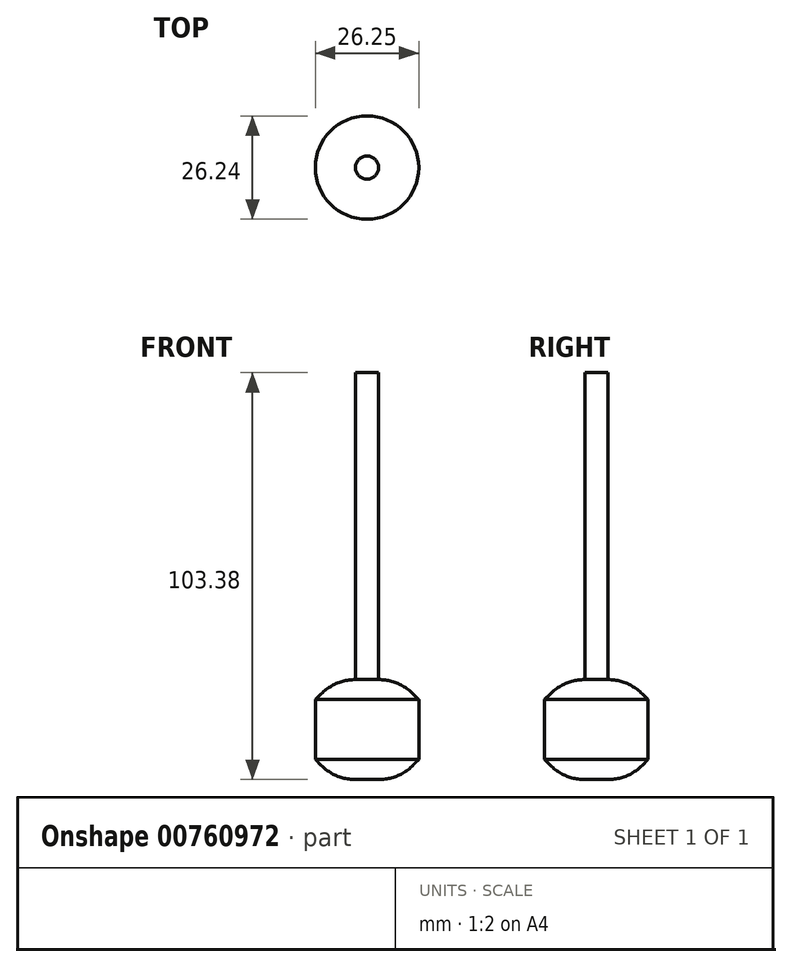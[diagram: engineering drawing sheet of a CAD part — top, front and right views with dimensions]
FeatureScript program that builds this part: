
annotation { "Feature Type Name" : "Feature", "Feature Type Description" : "" }
export const myFeature = defineFeature(function(context is Context, id is Id, definition is map)
    precondition{}
    {
        {
            var Q0;
            Q0=qCreatedBy(makeId("Top.planeOp"),FACE);
            var sketch = newSketch(context, id + "F0", { "sketchPlane" : qUnion([Q0])});
            skLineSegment(sketch, "E0.bottom", {"start": v(-19.37, 17.23) * mm, "end": v(32.22, 17.23) * mm});
            skLineSegment(sketch, "E0.top", {"start": v(-19.37, -26.96) * mm, "end": v(32.22, -26.96) * mm});
            skLineSegment(sketch, "E0.left", {"start": v(-19.37, 17.23) * mm, "end": v(-19.37, -26.96) * mm});
            skLineSegment(sketch, "E0.right", {"start": v(32.22, 17.23) * mm, "end": v(32.22, -26.96) * mm});
            skCircle(sketch, "E1", {"center": v(6.13, 1.85) * mm, "radius": 13.12 * mm});
            skSolve(sketch);
        }
        {
            var Q0;
            Q0=makeQuery(id+"F0.imprint","IMPRINT",FACE,{"disambiguationData":[TD([[makeQuery(id+"F0.imprint","IMPRINT",EDGE,{"derivedFrom":sQuery(id+"F0.wireOp",EDGE,"E1")}),1.0]])]});
            extrude(context, id + "F1", {"entities" : qUnion([Q0]), "depth" : 25.4 * mm, "offsetDistance" : 25.4 * mm});
        }
        {
            var Q0;
            Q0=makeQuery(id+"F1.opExtrude","CAP_EDGE",EDGE,{"disambiguationData":[OSD([sQuery(id+"F0.wireOp",EDGE,"E1")])],"isStart":false});
            var Q1;
            Q1=makeQuery(id+"F1.opExtrude","CAP_FACE",FACE,{"disambiguationData":[OSD([sQuery(id+"F0.wireOp",EDGE,"E1")])],"isStart":true});
            chamfer(context, id + "F2", {"entities" : qUnion([Q0, Q1]), "width" : 5.08 * mm, "tangentPropagation" : true});
        }
        {
            var Q0;
            {var subQ0=sQuery(id+"F0.wireOp",EDGE,"E1");Q0=makeQuery(id+"F2.opChamfer","BLEND_EDGE",EDGE,{"blendedFrom":[makeQuery(id+"F1.opExtrude","CAP_EDGE",EDGE,{"disambiguationData":[OSD([subQ0])],"isStart":false}),makeQuery(id+"F1.opExtrude","CAP_FACE",FACE,{"disambiguationData":[OSD([subQ0])],"isStart":false})],"blendedInto":[makeQuery(id+"F1.opExtrude","CAP_FACE",FACE,{"disambiguationData":[OSD([subQ0])],"isStart":false})]});}
            fillet(context, id + "F3", {"entities" : qUnion([Q0]), "radius" : 12.33 * mm, "tangentPropagation" : true, "allowEdgeOverflow" : false});
        }
        {
            var Q0;
            Q0=makeQuery(id+"F1.opExtrude","CAP_FACE",FACE,{"disambiguationData":[OSD([sQuery(id+"F0.wireOp",EDGE,"E1")])],"isStart":false});
            extrude(context, id + "F4", {"entities" : qUnion([Q0]), "operationType" : NewBodyOperationType.ADD, "depth" : 25.4 * mm, "offsetDistance" : 25.4 * mm});
        }
        {
            var Q0;
            Q0=makeQuery(id+"F4.opExtrude","CAP_FACE",FACE,{"disambiguationData":[OSD([sQuery(id+"F0.wireOp",EDGE,"E1")])],"isStart":false});
            extrude(context, id + "F5", {"entities" : qUnion([Q0]), "operationType" : NewBodyOperationType.ADD, "depth" : 52.58 * mm, "offsetDistance" : 25.4 * mm});
        }
        {
            var Q0;
            {var subQ0=sQuery(id+"F0.wireOp",EDGE,"E1");Q0=makeQuery(id+"F2.opChamfer","BLEND_EDGE",EDGE,{"blendedFrom":[makeQuery(id+"F1.opExtrude","CAP_EDGE",EDGE,{"disambiguationData":[OSD([subQ0])],"isStart":true}),makeQuery(id+"F1.opExtrude","CAP_FACE",FACE,{"disambiguationData":[OSD([subQ0])],"isStart":true})],"blendedInto":[makeQuery(id+"F1.opExtrude","CAP_FACE",FACE,{"disambiguationData":[OSD([subQ0])],"isStart":true})]});}
            fillet(context, id + "F6", {"entities" : qUnion([Q0]), "radius" : 12.33 * mm, "tangentPropagation" : true, "allowEdgeOverflow" : false});
        }
    });
